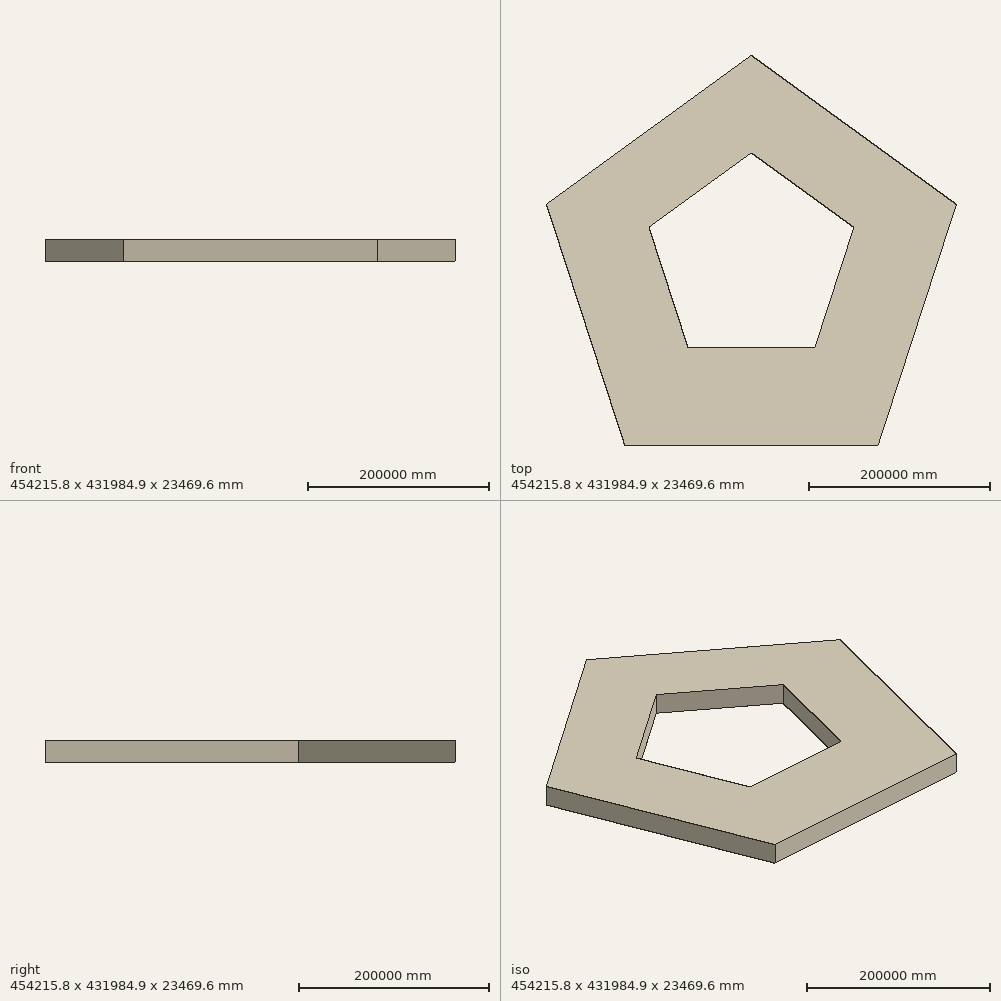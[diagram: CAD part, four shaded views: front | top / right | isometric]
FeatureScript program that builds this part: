
annotation { "Feature Type Name" : "Feature", "Feature Type Description" : "" }
export const myFeature = defineFeature(function(context is Context, id is Id, definition is map)
    precondition{}
    {
        {
            var Q0;
            Q0=qCreatedBy(makeId("Top.planeOp"),FACE);
            var sketch = newSketch(context, id + "F0", { "sketchPlane" : qUnion([Q0])});
            skLineSegment(sketch, "E0", {"start": v(-70180.2, -107996.17) * mm, "end": v(70180.2, -107996.17) * mm});
            skLineSegment(sketch, "E1", {"start": v(70180.2, -107996.17) * mm, "end": v(113553.95, 25494.5) * mm});
            skLineSegment(sketch, "E2", {"start": v(113553.95, 25494.5) * mm, "end": v(0, 107996.28) * mm});
            skLineSegment(sketch, "E3", {"start": v(0, 107996.28) * mm, "end": v(-113553.95, 25494.5) * mm});
            skLineSegment(sketch, "E4", {"start": v(-113553.95, 25494.5) * mm, "end": v(-70180.2, -107996.17) * mm});
            skLineSegment(sketch, "E5", {"start": v(0, 215992.4) * mm, "end": v(-227107.9, 50988.86) * mm});
            skLineSegment(sketch, "E6", {"start": v(-227107.9, 50988.86) * mm, "end": v(-140360.4, -215992.49) * mm});
            skLineSegment(sketch, "E7", {"start": v(-140360.4, -215992.49) * mm, "end": v(140360.4, -215992.49) * mm});
            skLineSegment(sketch, "E8", {"start": v(140360.4, -215992.49) * mm, "end": v(227107.9, 50988.86) * mm});
            skLineSegment(sketch, "E9", {"start": v(0, 215992.4) * mm, "end": v(227107.9, 50988.86) * mm});
            skSolve(sketch);
        }
        {
            var Q0;
            Q0 = qSketchRegion(id + "F0", true);
            extrude(context, id + "F1", {"entities" : qUnion([Q0]), "depth" : 23469.6 * mm, "offsetDistance" : 30.48 * mm});
        }
        {
            var Q0;
            Q0=makeQuery(id+"F0.imprint","IMPRINT",FACE,{"disambiguationData":[TD([[makeQuery(id+"F0.imprint","IMPRINT",EDGE,{"derivedFrom":sQuery(id+"F0.wireOp",EDGE,"E0")}),-1.0]])]});
            extrude(context, id + "F2", {"entities" : qUnion([Q0]), "operationType" : NewBodyOperationType.ADD, "depth" : 23469.6 * mm, "offsetDistance" : 30.48 * mm});
        }
    });
